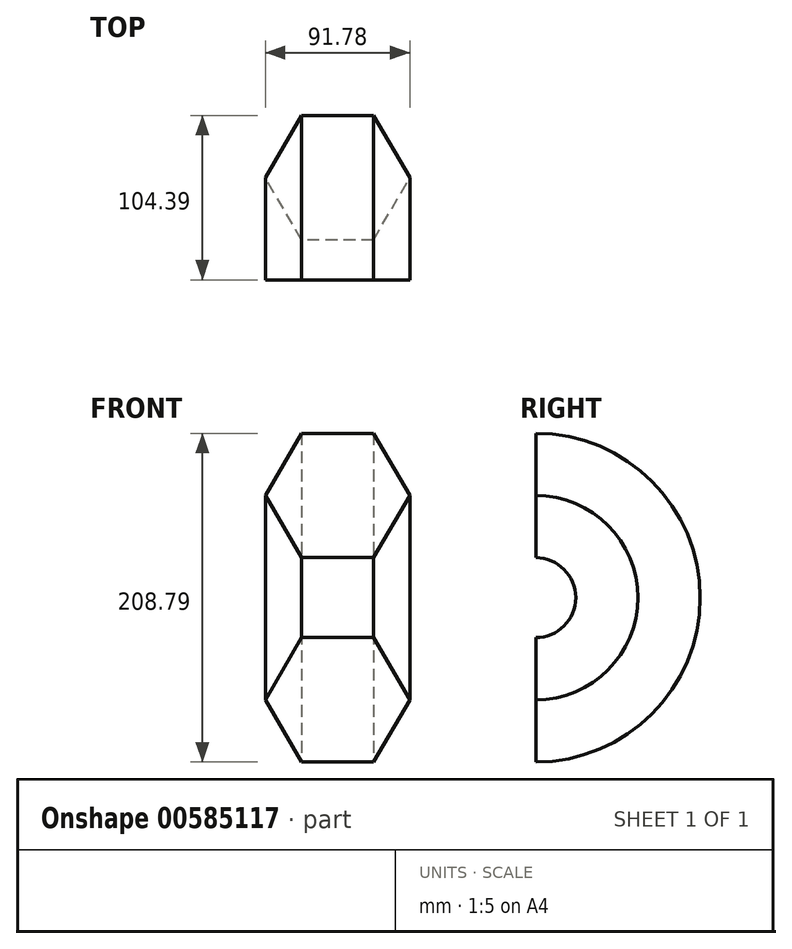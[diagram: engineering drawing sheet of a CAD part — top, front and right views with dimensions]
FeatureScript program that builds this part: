
annotation { "Feature Type Name" : "Feature", "Feature Type Description" : "" }
export const myFeature = defineFeature(function(context is Context, id is Id, definition is map)
    precondition{}
    {
        {
            var Q0;
            Q0=qCreatedBy(makeId("Front.planeOp"),FACE);
            var sketch = newSketch(context, id + "F0", { "sketchPlane" : qUnion([Q0])});
            skLineSegment(sketch, "E0", {"start": v(-48.83, 0) * mm, "end": v(-25.8, 39.5) * mm});
            skLineSegment(sketch, "E1", {"start": v(-25.8, 39.5) * mm, "end": v(19.92, 39.5) * mm});
            skLineSegment(sketch, "E2", {"start": v(19.92, 39.5) * mm, "end": v(42.95, 0) * mm});
            skLineSegment(sketch, "E3", {"start": v(42.95, 0) * mm, "end": v(-48.83, 0) * mm});
            skLineSegment(sketch, "E4", {"start": v(-48.83, 0) * mm, "end": v(-25.8, -39.5) * mm});
            skLineSegment(sketch, "E5", {"start": v(-25.8, -39.5) * mm, "end": v(19.92, -39.5) * mm});
            skLineSegment(sketch, "E6", {"start": v(19.92, -39.5) * mm, "end": v(42.95, 0) * mm});
            skSolve(sketch);
        }
        {
            var Q0;
            Q0=qCreatedBy(makeId("Front.planeOp"),FACE);
            var sketch = newSketch(context, id + "F1", { "sketchPlane" : qUnion([Q0])});
            skLineSegment(sketch, "E7", {"start": v(-78.26, 64.9) * mm, "end": v(73.25, 64.9) * mm});
            skSolve(sketch);
        }
        {
            var Q0;
            Q0=makeQuery(id+"F0.imprint","IMPRINT",FACE,{"disambiguationData":[TD([[makeQuery(id+"F0.imprint","IMPRINT",EDGE,{"derivedFrom":sQuery(id+"F0.wireOp",EDGE,"E3")}),1.0]])]});
            var Q1;
            Q1=makeQuery(id+"F0.imprint","IMPRINT",FACE,{"disambiguationData":[TD([[makeQuery(id+"F0.imprint","IMPRINT",EDGE,{"derivedFrom":sQuery(id+"F0.wireOp",EDGE,"E0")}),-1.0]])]});
            var Q2;
            Q2=sQuery(id+"F1.wireOp",EDGE,"E7");
            revolve(context, id + "F2", {"entities" : qUnion([Q0, Q1]), "axis" : qUnion([Q2]), "revolveType" : RevolveType.ONE_DIRECTION, "angle" : 180 * degree});
        }
    });
